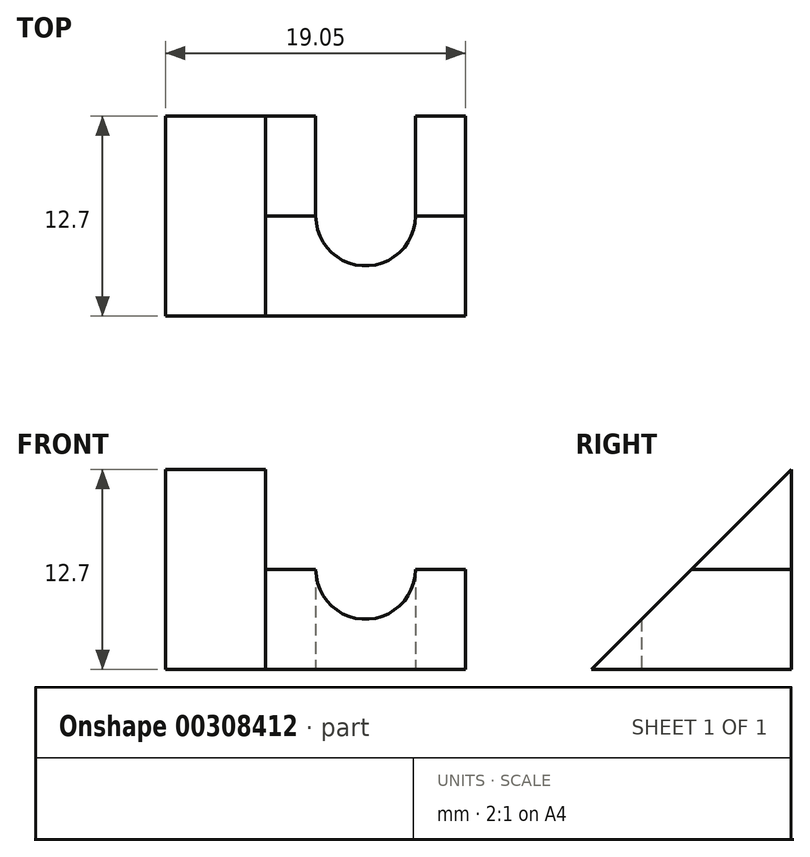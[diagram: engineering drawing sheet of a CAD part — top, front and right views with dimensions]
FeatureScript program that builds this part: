
annotation { "Feature Type Name" : "Feature", "Feature Type Description" : "" }
export const myFeature = defineFeature(function(context is Context, id is Id, definition is map)
    precondition{}
    {
        {
            var Q0;
            Q0=qCreatedBy(makeId("Top.planeOp"),FACE);
            var sketch = newSketch(context, id + "F0", { "sketchPlane" : qUnion([Q0])});
            skLineSegment(sketch, "E0.bottom", {"start": v(0, 0) * mm, "end": v(19.05, 0) * mm});
            skLineSegment(sketch, "E0.top", {"start": v(0, 25.4) * mm, "end": v(38.1, 25.4) * mm});
            skLineSegment(sketch, "E0.left", {"start": v(0, 0) * mm, "end": v(0, 25.4) * mm});
            skLineSegment(sketch, "E0.right", {"start": v(38.1, 12.7) * mm, "end": v(38.1, 25.4) * mm});
            skLineSegment(sketch, "E1", {"start": v(6.35, 25.4) * mm, "end": v(6.35, 0) * mm});
            skLineSegment(sketch, "E2", {"start": v(19.05, 25.4) * mm, "end": v(19.05, 0) * mm});
            skLineSegment(sketch, "E3", {"start": v(19.05, 12.7) * mm, "end": v(38.1, 12.7) * mm});
            skLineSegment(sketch, "E4", {"start": v(12.7, 19.05) * mm, "end": v(12.7, 6.35) * mm, "construction": true});
            skArc(sketch, "E5.0.startCap", {"start": v(9.52, 19.05) * mm, "mid": v(12.7, 22.23) * mm, "end": v(15.88, 19.05) * mm});
            skArc(sketch, "E5.0.endCap", {"start": v(15.88, 6.35) * mm, "mid": v(12.7, 3.18) * mm, "end": v(9.52, 6.35) * mm});
            skLineSegment(sketch, "E5.0.left", {"start": v(15.88, 19.05) * mm, "end": v(15.88, 6.35) * mm});
            skLineSegment(sketch, "E5.0.right", {"start": v(9.52, 19.05) * mm, "end": v(9.52, 6.35) * mm});
            skSolve(sketch);
        }
        {
            var Q0;
            {var subQ0=sQuery(id+"F0.wireOp",EDGE,"E0.left");Q0=makeQuery(id+"F0.imprint","IMPRINT",FACE,{"disambiguationData":[TD([[makeQuery(id+"F0.imprint","IMPRINT",EDGE,{"derivedFrom":subQ0}),-1.0]])]});}
            extrude(context, id + "F1", {"entities" : qUnion([Q0]), "depth" : 25.4 * mm});
        }
        {
            var Q0;
            {var subQ0=sQuery(id+"F0.wireOp",EDGE,"E0.right");Q0=makeQuery(id+"F0.imprint","IMPRINT",FACE,{"disambiguationData":[TD([[makeQuery(id+"F0.imprint","IMPRINT",EDGE,{"derivedFrom":subQ0}),1.0]])]});}
            extrude(context, id + "F2", {"entities" : qUnion([Q0]), "depth" : 25.4 * mm});
        }
        {
            var Q0;
            {var subQ0=sQuery(id+"F0.wireOp",EDGE,"E1");Q0=makeQuery(id+"F0.imprint","IMPRINT",FACE,{"disambiguationData":[TD([[makeQuery(id+"F0.imprint","IMPRINT",EDGE,{"derivedFrom":subQ0}),1.0]])]});}
            extrude(context, id + "F3", {"entities" : qUnion([Q0]), "depth" : 6.35 * mm});
        }
        {
            var Q0;
            Q0=makeQuery(id+"F1.opExtrude","SWEPT_FACE",FACE,{"disambiguationData":[OSD([sQuery(id+"F0.wireOp",EDGE,"E0.left")])]});
            var sketch = newSketch(context, id + "F4", { "sketchPlane" : qUnion([Q0])});
            skLineSegment(sketch, "E6", {"start": v(-25.4, 0) * mm, "end": v(-12.7, 0) * mm});
            skPoint(sketch, "E7.endSnap0", {"position": v(0, 12.7) * mm});
            skLineSegment(sketch, "E8", {"start": v(-25.4, 25.4) * mm, "end": v(0, 0) * mm});
            skSolve(sketch);
        }
        {
            var Q0;
            Q0=makeQuery(id+"F4.imprint","IMPRINT",FACE,{"disambiguationData":[TD([[makeQuery(id+"F4.imprint","IMPRINT",EDGE,{"derivedFrom":sQuery(id+"F4.wireOp",EDGE,"E8")}),1.0]])]});
            extrude(context, id + "F5", {"entities" : qUnion([Q0]), "operationType" : NewBodyOperationType.REMOVE, "endBound" : BoundingType.THROUGH_ALL, "oppositeDirection" : true, "depth" : 38.1 * mm});
        }
        {
            var Q0;
            Q0=makeQuery(id+"F2.opExtrude","SWEPT_FACE",FACE,{"disambiguationData":[OSD([sQuery(id+"F0.wireOp",EDGE,"E0.right")])]});
            var sketch = newSketch(context, id + "F6", { "sketchPlane" : qUnion([Q0])});
            skLineSegment(sketch, "E9", {"start": v(12.7, 0) * mm, "end": v(12.7, 12.7) * mm});
            skLineSegment(sketch, "E10", {"start": v(12.7, 12.7) * mm, "end": v(25.4, 25.4) * mm});
            skSolve(sketch);
        }
        {
            var Q0;
            {var subQ0=sQuery(id+"F6.wireOp",EDGE,"E10");Q0=makeQuery(id+"F6.imprint","IMPRINT",FACE,{"disambiguationData":[TD([[makeQuery(id+"F6.imprint","IMPRINT",EDGE,{"derivedFrom":subQ0}),1.0]])]});}
            extrude(context, id + "F7", {"entities" : qUnion([Q0]), "operationType" : NewBodyOperationType.REMOVE, "endBound" : BoundingType.THROUGH_ALL, "oppositeDirection" : true, "depth" : 25.4 * mm});
        }
    });
